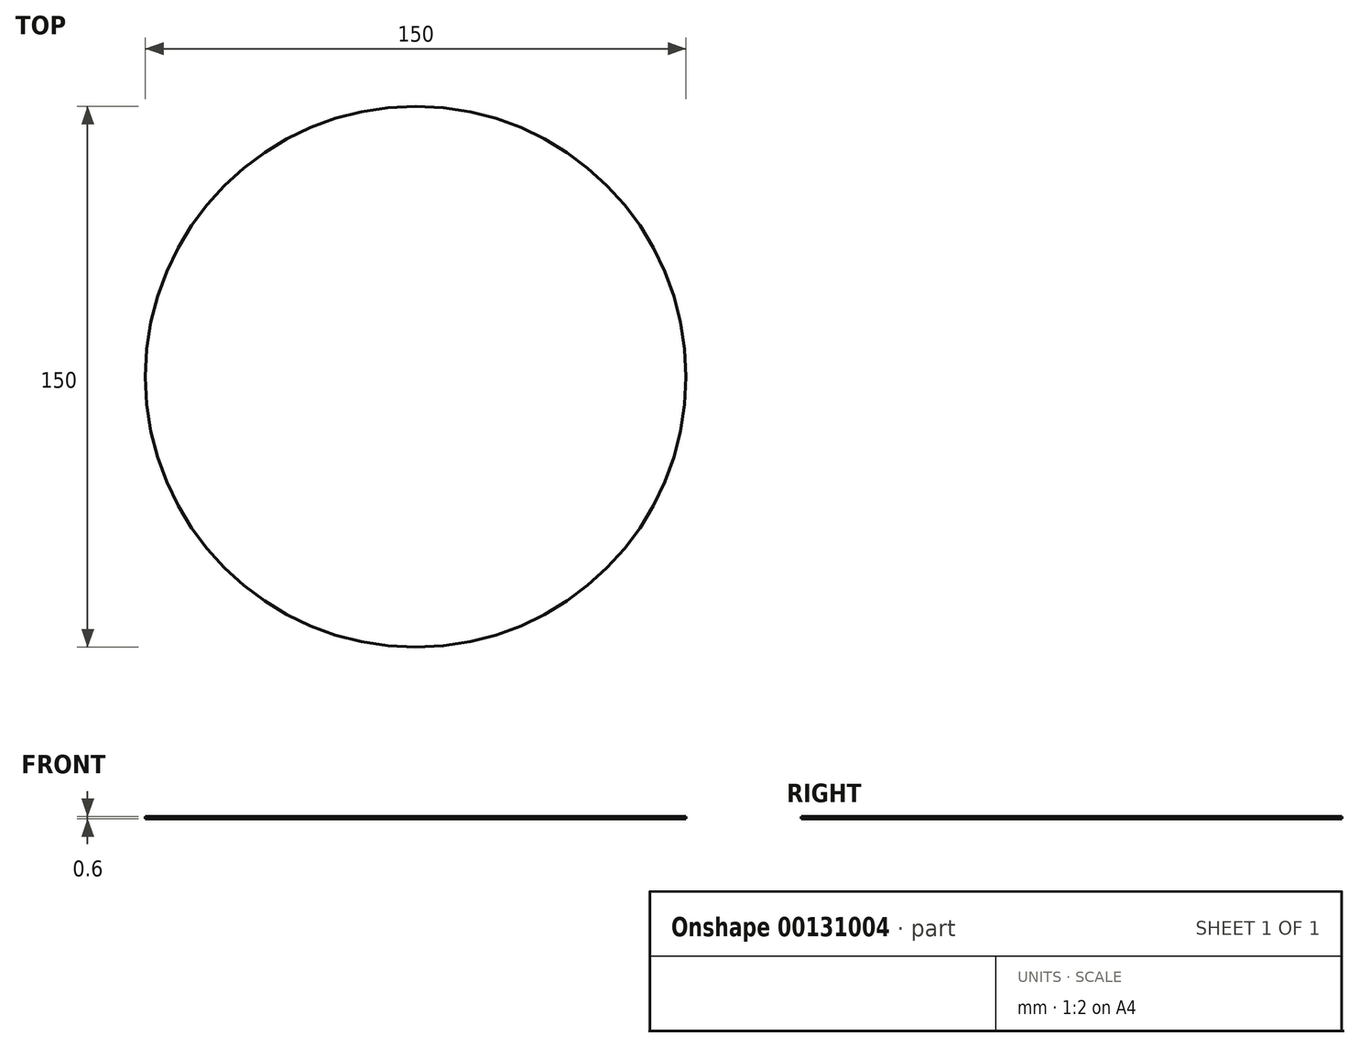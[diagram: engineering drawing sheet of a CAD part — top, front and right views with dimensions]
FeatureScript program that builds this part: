
annotation { "Feature Type Name" : "Feature", "Feature Type Description" : "" }
export const myFeature = defineFeature(function(context is Context, id is Id, definition is map)
    precondition{}
    {
        {
            var Q0;
            Q0=qCreatedBy(makeId("Top.planeOp"),FACE);
            var sketch = newSketch(context, id + "F0", { "sketchPlane" : qUnion([Q0])});
            skCircle(sketch, "E0", {"center": v(0, 0) * mm, "radius": 75 * mm});
            skSolve(sketch);
        }
        {
            var Q0;
            Q0=makeQuery(id+"F0.imprint","IMPRINT",FACE,{"disambiguationData":[TD([[makeQuery(id+"F0.imprint","IMPRINT",EDGE,{"derivedFrom":sQuery(id+"F0.wireOp",EDGE,"E0")}),1.0]])]});
            extrude(context, id + "F1", {"entities" : qUnion([Q0]), "depth" : .6 * mm});
        }
    });
